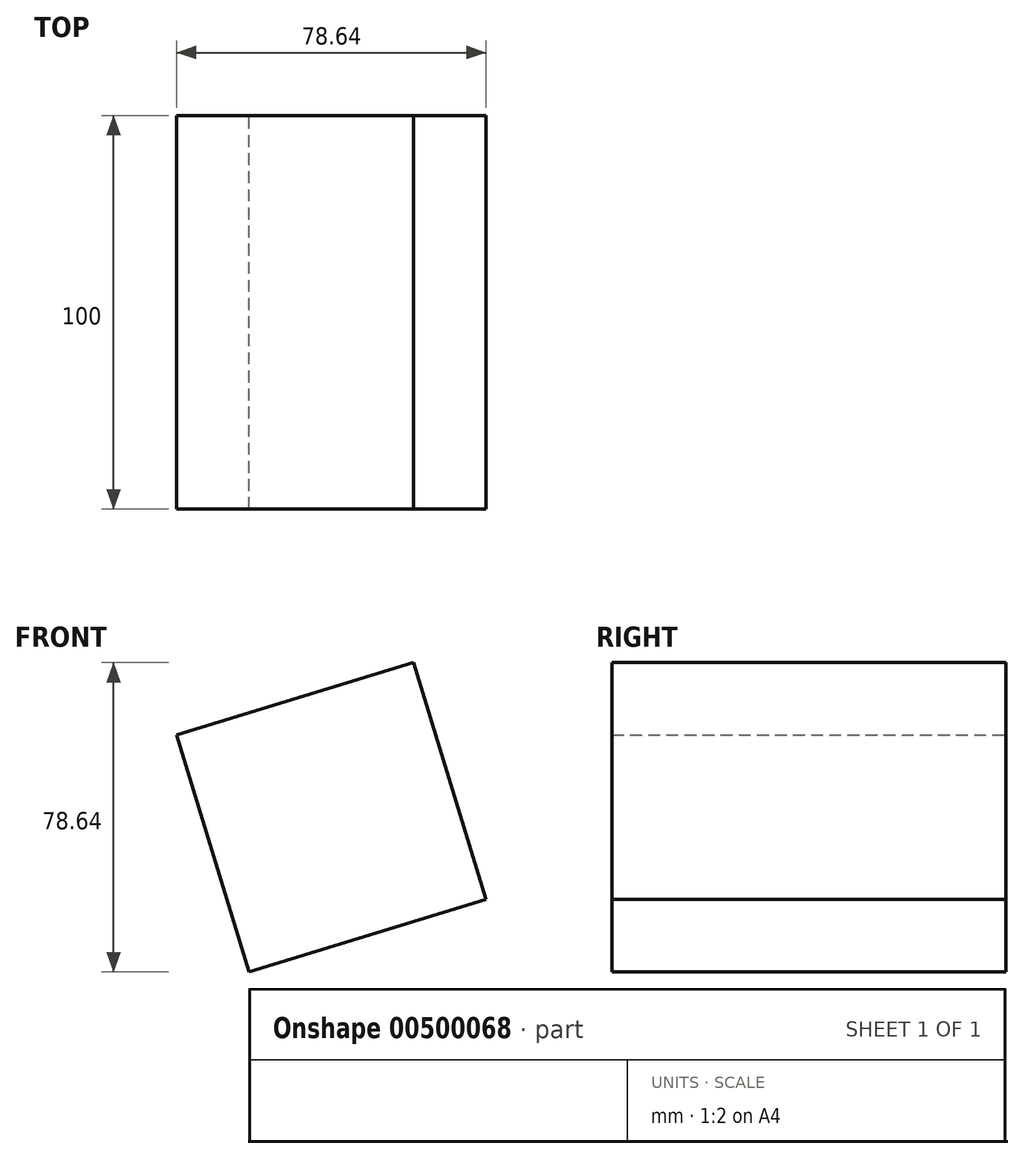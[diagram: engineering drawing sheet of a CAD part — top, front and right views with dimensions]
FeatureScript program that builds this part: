
annotation { "Feature Type Name" : "Feature", "Feature Type Description" : "" }
export const myFeature = defineFeature(function(context is Context, id is Id, definition is map)
    precondition{}
    {
        {
            var Q0;
            Q0=qCreatedBy(makeId("Front.planeOp"),FACE);
            var sketch = newSketch(context, id + "F0", { "sketchPlane" : qUnion([Q0])});
            skCircle(sketch, "E0.cCircle", {"center": v(0, 0) * mm, "radius": 44.52 * mm, "construction": true});
            skLineSegment(sketch, "E0.0", {"start": v(39.32, -20.88) * mm, "end": v(-20.88, -39.32) * mm});
            skLineSegment(sketch, "E0.1", {"start": v(-20.88, -39.32) * mm, "end": v(-39.32, 20.88) * mm});
            skLineSegment(sketch, "E0.2", {"start": v(-39.32, 20.88) * mm, "end": v(20.88, 39.32) * mm});
            skLineSegment(sketch, "E0.3", {"start": v(20.88, 39.32) * mm, "end": v(39.32, -20.88) * mm});
            skSolve(sketch);
        }
        {
            var Q0;
            Q0=makeQuery(id+"F0.imprint","IMPRINT",FACE,{"disambiguationData":[TD([[makeQuery(id+"F0.imprint","IMPRINT",EDGE,{"derivedFrom":sQuery(id+"F0.wireOp",EDGE,"E0.0")}),-1.0]])]});
            extrude(context, id + "F1", {"entities" : qUnion([Q0]), "endBound" : BoundingType.SYMMETRIC, "depth" : 100 * mm});
        }
    });
